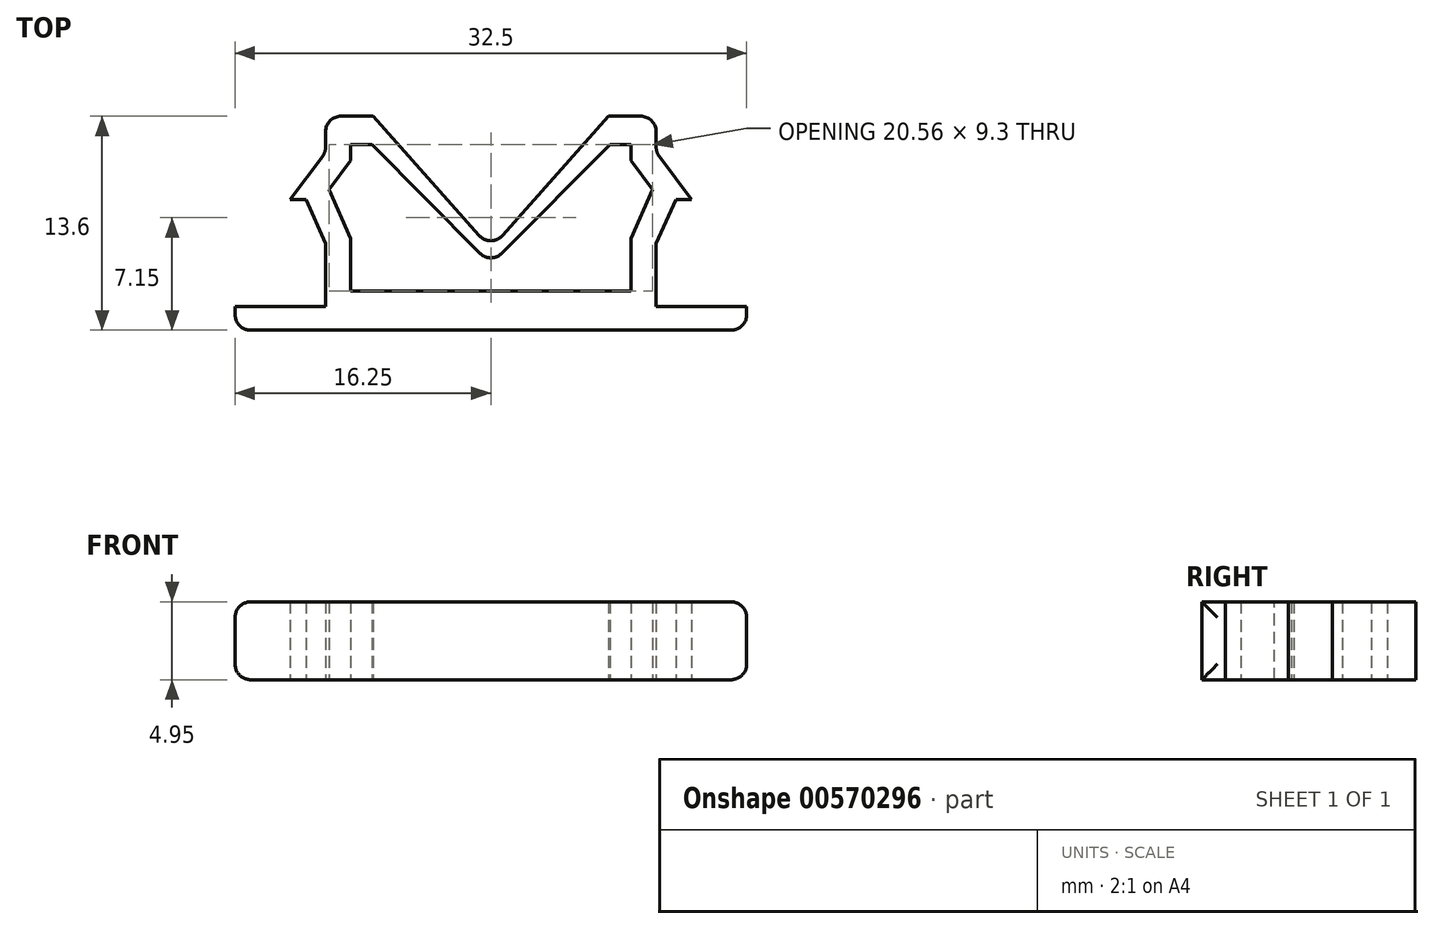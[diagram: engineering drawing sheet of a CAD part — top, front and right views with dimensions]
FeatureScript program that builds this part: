
annotation { "Feature Type Name" : "Feature", "Feature Type Description" : "" }
export const myFeature = defineFeature(function(context is Context, id is Id, definition is map)
    precondition{}
    {
        {
            var Q0;
            Q0=qCreatedBy(makeId("Top.planeOp"),FACE);
            var sketch = newSketch(context, id + "F0", { "sketchPlane" : qUnion([Q0])});
            skLineSegment(sketch, "E0", {"start": v(0, 0) * mm, "end": v(-16.25, 0) * mm});
            skLineSegment(sketch, "E1", {"start": v(-16.25, 0) * mm, "end": v(-16.25, 1.5) * mm});
            skLineSegment(sketch, "E2", {"start": v(-16.25, 1.5) * mm, "end": v(-10.5, 1.5) * mm});
            skLineSegment(sketch, "E3", {"start": v(-10.5, 1.5) * mm, "end": v(-10.5, 5.5) * mm});
            skLineSegment(sketch, "E4", {"start": v(-10.5, 5.5) * mm, "end": v(-11.75, 8.3) * mm});
            skLineSegment(sketch, "E5", {"start": v(-12.75, 8.3) * mm, "end": v(-10.5, 11.3) * mm});
            skLineSegment(sketch, "E6", {"start": v(-10.5, 11.3) * mm, "end": v(-10.5, 13.6) * mm});
            skLineSegment(sketch, "E7", {"start": v(-11.75, 8.3) * mm, "end": v(-12.75, 8.3) * mm});
            skLineSegment(sketch, "E8", {"start": v(0, 10.36) * mm, "end": v(0, 0) * mm, "construction": true});
            skLineSegment(sketch, "E9.1", {"start": v(-8.9, 10.77) * mm, "end": v(-8.9, 11.8) * mm});
            skLineSegment(sketch, "E9.2", {"start": v(0, 2.5) * mm, "end": v(-8.9, 2.5) * mm});
            skLineSegment(sketch, "E9.3", {"start": v(-8.9, 2.5) * mm, "end": v(-8.9, 5.84) * mm});
            skLineSegment(sketch, "E9.4", {"start": v(-8.9, 5.84) * mm, "end": v(-10.28, 8.93) * mm});
            skLineSegment(sketch, "E9.5", {"start": v(-10.28, 8.93) * mm, "end": v(-8.9, 10.77) * mm});
            skLineSegment(sketch, "E10.MirrorCS", {"start": v(10.28, 8.93) * mm, "end": v(8.9, 10.77) * mm});
            skLineSegment(sketch, "E11.MirrorCS", {"start": v(11.75, 8.3) * mm, "end": v(12.75, 8.3) * mm});
            skLineSegment(sketch, "E12.MirrorCS", {"start": v(8.9, 10.77) * mm, "end": v(8.9, 11.8) * mm});
            skLineSegment(sketch, "E13.MirrorCS", {"start": v(12.75, 8.3) * mm, "end": v(10.5, 11.3) * mm});
            skLineSegment(sketch, "E14.MirrorCS", {"start": v(10.5, 11.3) * mm, "end": v(10.5, 13.6) * mm});
            skLineSegment(sketch, "E15.MirrorCS", {"start": v(8.9, 5.84) * mm, "end": v(10.28, 8.93) * mm});
            skLineSegment(sketch, "E16.MirrorCS", {"start": v(16.25, 1.5) * mm, "end": v(10.5, 1.5) * mm});
            skLineSegment(sketch, "E17.MirrorCS", {"start": v(16.25, 0) * mm, "end": v(16.25, 1.5) * mm});
            skLineSegment(sketch, "E18.MirrorCS", {"start": v(10.5, 5.5) * mm, "end": v(11.75, 8.3) * mm});
            skLineSegment(sketch, "E19.MirrorCS", {"start": v(10.5, 1.5) * mm, "end": v(10.5, 5.5) * mm});
            skLineSegment(sketch, "E20.MirrorCS", {"start": v(8.9, 2.5) * mm, "end": v(8.9, 5.84) * mm});
            skLineSegment(sketch, "E21.MirrorCS", {"start": v(0, 2.5) * mm, "end": v(8.9, 2.5) * mm});
            skLineSegment(sketch, "E22.MirrorCS", {"start": v(0, 0) * mm, "end": v(16.25, 0) * mm});
            skLineSegment(sketch, "E23", {"start": v(-10.5, 13.6) * mm, "end": v(-7.48, 13.6) * mm});
            skLineSegment(sketch, "E24", {"start": v(-7.48, 13.6) * mm, "end": v(0, 5.18) * mm});
            skLineSegment(sketch, "E25.0", {"start": v(-7.55, 11.8) * mm, "end": v(0, 4.18) * mm});
            skLineSegment(sketch, "E26", {"start": v(-7.55, 11.8) * mm, "end": v(-8.9, 11.8) * mm});
            skLineSegment(sketch, "E27.MirrorCS", {"start": v(10.5, 13.6) * mm, "end": v(7.48, 13.6) * mm});
            skLineSegment(sketch, "E28.MirrorCS", {"start": v(7.48, 13.6) * mm, "end": v(0, 5.18) * mm});
            skLineSegment(sketch, "E29.MirrorCS", {"start": v(7.55, 11.8) * mm, "end": v(0, 4.18) * mm});
            skLineSegment(sketch, "E30.MirrorCS", {"start": v(7.55, 11.8) * mm, "end": v(8.9, 11.8) * mm});
            skSolve(sketch);
        }
        {
            var Q0;
            Q0 = qSketchRegion(id + "F0", true);
            extrude(context, id + "F1", {"entities" : qUnion([Q0]), "depth" : 4.95 * mm, "offsetDistance" : 25 * mm});
        }
        {
            var Q0;
            Q0=makeQuery(id+"F1.opExtrude","CAP_EDGE",EDGE,{"disambiguationData":[OSD([sQuery(id+"F0.wireOp",EDGE,"E1")])],"isStart":false});
            var Q1;
            Q1=makeQuery(id+"F1.opExtrude","CAP_EDGE",EDGE,{"disambiguationData":[OSD([sQuery(id+"F0.wireOp",EDGE,"E1")])],"isStart":true});
            var Q2;
            Q2=makeQuery(id+"F1.opExtrude","CAP_EDGE",EDGE,{"disambiguationData":[OSD([sQuery(id+"F0.wireOp",EDGE,"E17.MirrorCS")])],"isStart":false});
            var Q3;
            Q3=makeQuery(id+"F1.opExtrude","CAP_EDGE",EDGE,{"disambiguationData":[OSD([sQuery(id+"F0.wireOp",EDGE,"E17.MirrorCS")])],"isStart":true});
            var Q4;
            Q4=makeQuery(id+"F1.opExtrude","SWEPT_EDGE",EDGE,{"disambiguationData":[OSD([sQuery(id+"F0.wireOp",EDGE,"E6"),sQuery(id+"F0.wireOp",EDGE,"VBFfd1g8-y1CK-OYXq-Jd71-TZBDZbHSDFq2")])]});
            var Q5;
            Q5=makeQuery(id+"F1.opExtrude","SWEPT_EDGE",EDGE,{"disambiguationData":[OSD([sQuery(id+"F0.wireOp",EDGE,"E14.MirrorCS"),sQuery(id+"F0.wireOp",EDGE,"0804b22a-e127-4b93-bc7e-1eb8c15297ee0.MirrorCS")])]});
            var Q6;
            Q6=makeQuery(id+"F1.opExtrude","SWEPT_EDGE",EDGE,{"disambiguationData":[OSD([sQuery(id+"F0.wireOp",EDGE,"E0"),sQuery(id+"F0.wireOp",EDGE,"E1")])]});
            var Q7;
            Q7=makeQuery(id+"F1.opExtrude","SWEPT_EDGE",EDGE,{"disambiguationData":[OSD([sQuery(id+"F0.wireOp",EDGE,"E17.MirrorCS"),sQuery(id+"F0.wireOp",EDGE,"E22.MirrorCS")])]});
            var Q8;
            Q8=makeQuery(id+"F1.opExtrude","SWEPT_EDGE",EDGE,{"disambiguationData":[OSD([sQuery(id+"F0.wireOp",EDGE,"E24"),sQuery(id+"F0.wireOp",EDGE,"E28.MirrorCS")])]});
            var Q9;
            Q9=makeQuery(id+"F1.opExtrude","SWEPT_EDGE",EDGE,{"disambiguationData":[OSD([sQuery(id+"F0.wireOp",EDGE,"E25.0"),sQuery(id+"F0.wireOp",EDGE,"E29.MirrorCS")])]});
            fillet(context, id + "F2", {"entities" : qUnion([Q0, Q1, Q2, Q3, Q4, Q5, Q6, Q7, Q8, Q9]), "radius" : 1 * mm, "tangentPropagation" : true, "allowEdgeOverflow" : false});
        }
    });
